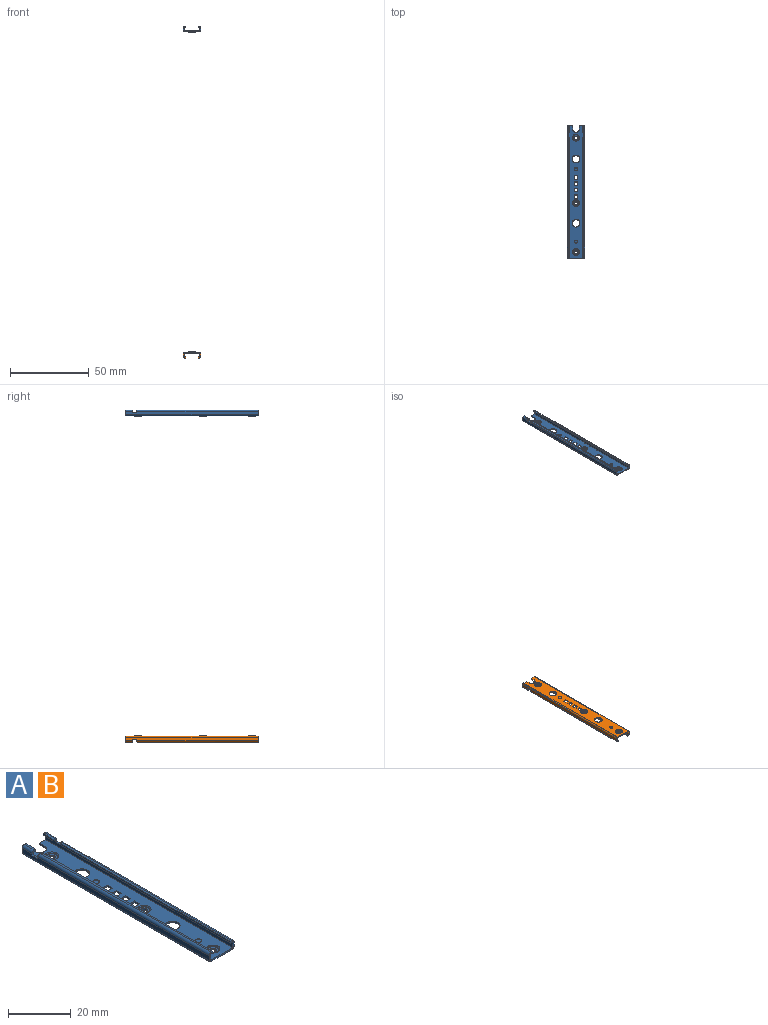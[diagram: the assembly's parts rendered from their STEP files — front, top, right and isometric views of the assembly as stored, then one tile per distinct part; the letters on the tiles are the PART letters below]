
ASSEMBLY  parts=2 mates=1
PART A: 85 faces, bbox 11.2x84.3x4 mm
  f0: plane 84.3x1.75mm, normal (-1,0,0), area 145.8mm2, adj f13,f14,f22,f51,f78,f79,f82,f84
  f1: plane 84.3x2.29mm, normal (1,0,0), area 190.3mm2, adj f2,f9,f22,f24,f78,f79,f82,f84
  f2: plane 84.3x9.9mm, normal (0,0,1), area 706.3mm2, adj f1,f10,f18,f22,f26,f27,f28,f29
  f3: plane 84.3x9.6mm, normal (0,0,-1), area 681.4mm2, adj f14,f18,f22,f26,f27,f28,f29,f30
  f4: plane 84.3x1.75mm, normal (1,0,0), area 145.8mm2, adj f12,f18,f49,f50,f80,f81,f83,f84
  f5: plane 76.91x0.7mm, normal (0,0,1), area 53.6mm2, adj f8,f13,f82,f84
  f6: plane 76.91x0.7mm, normal (0,0,1), area 53.6mm2, adj f7,f12,f83,f84
  f7: plane 75.54x0.66mm, normal (-1,0,0), area 49.9mm2, adj f6,f11,f83,f84
  f8: plane 75.54x0.66mm, normal (1,0,0), area 49.9mm2, adj f5,f9,f82,f84
  f9: plane 77.11x1.05mm, normal (0,0,-1), area 80.5mm2, adj f1,f8,f82,f84
  f10: plane 84.3x2.29mm, normal (-1,0,0), area 190.3mm2, adj f2,f11,f18,f25,f80,f81,f83,f84
  f11: plane 77.11x1.05mm, normal (0,0,-1), area 80.5mm2, adj f7,f10,f83,f84
  f12: cylinder r=1mm len=77.24mm, axis (0,-1,0), area 121.2mm2, adj f4,f6,f83,f84
  f13: cylinder r=1mm len=77.24mm, axis (0,1,0), area 121.2mm2, adj f0,f5,f82,f84
  f14: cylinder r=0.8mm len=84.3mm, axis (0,-1,0), area 105.9mm2, adj f0,f3,f22,f84
  f15: cylinder r=1.07mm len=2.14mm, axis (0,0,1), area 4mm2, adj f35,f44
  f16: cylinder r=1.07mm len=2.14mm, axis (0,0,1), area 4mm2, adj f33,f42
  f17: cylinder r=1.07mm len=2.14mm, axis (0,0,1), area 4mm2, adj f31,f40
  f18: plane 3.55x3.44mm, normal (0,1,0), area 4.3mm2, adj f2,f3,f4,f10,f19,f23,f25,f26
  f19: plane 4.45x0.66mm, normal (-1,0,0), area 2.9mm2, adj f18,f23,f25,f81
  f20: plane 4.45x0.66mm, normal (1,0,0), area 2.9mm2, adj f21,f22,f24,f78
  f21: plane 4.45x0.7mm, normal (0,0,1), area 3.1mm2, adj f20,f22,f51,f78
  f22: plane 3.55x3.44mm, normal (0,1,0), area 4.3mm2, adj f0,f1,f2,f3,f14,f20,f21,f24
  f23: plane 4.45x0.7mm, normal (0,0,1), area 3.1mm2, adj f18,f19,f50,f81
  f24: plane 4.45x1.05mm, normal (0,0,-1), area 4.7mm2, adj f1,f20,f22,f78
  f25: plane 4.45x1.05mm, normal (0,0,-1), area 4.7mm2, adj f10,f18,f19,f81
  f26: plane 2.3x0.6mm, normal (-1,0,0), area 1.4mm2, adj f2,f3,f18,f28
  f27: plane 2.3x0.6mm, normal (1,0,0), area 1.4mm2, adj f2,f3,f22,f28
  f28: cylinder r=2.17mm len=4.33mm, axis (0,0,1), area 4.1mm2, adj f2,f3,f26,f27
  f29: cylinder r=2.46mm len=4.91mm, axis (0,0,1), area 9.3mm2, adj f2,f3
  f30: cylinder r=2.46mm len=4.91mm, axis (0,0,1), area 9.3mm2, adj f2,f3
  f31: plane 3.8x3.8mm, normal (0,0,-1), area 7.7mm2, adj f17,f39
  f32: cylinder r=2.2mm len=4.4mm, axis (0,0,1), area 2.5mm2, adj f3,f39
  f33: plane 3.8x3.8mm, normal (0,0,-1), area 7.7mm2, adj f16,f38
  f34: cylinder r=2.2mm len=4.4mm, axis (0,0,1), area 2.5mm2, adj f3,f38
  f35: plane 3.8x3.8mm, normal (0,0,-1), area 7.7mm2, adj f15,f37
  f36: cylinder r=2.2mm len=4.4mm, axis (0,0,1), area 2.5mm2, adj f3,f37
  f37: torus R=1.9mm, axis (0,0,-1), area 6.2mm2, adj f35,f36
  f38: torus R=1.9mm, axis (0,0,-1), area 6.2mm2, adj f33,f34
  f39: torus R=1.9mm, axis (0,0,-1), area 6.2mm2, adj f31,f32
  f40: plane 3.81x3.81mm, normal (0,0,1), area 7.8mm2, adj f17,f41
  f41: cylinder r=1.91mm len=3.81mm, axis (0,0,1), area 2.2mm2, adj f40,f48
  f42: plane 3.81x3.81mm, normal (0,0,1), area 7.8mm2, adj f16,f43
  f43: cylinder r=1.91mm len=3.81mm, axis (0,0,1), area 2.2mm2, adj f42,f47
  f44: plane 3.81x3.81mm, normal (0,0,1), area 7.8mm2, adj f15,f45
  f45: cylinder r=1.91mm len=3.81mm, axis (0,0,1), area 2.2mm2, adj f44,f46
  f46: torus R=2.21mm, axis (0,0,1), area 6mm2, adj f2,f45
  f47: torus R=2.21mm, axis (0,0,1), area 6mm2, adj f2,f43
  f48: torus R=2.21mm, axis (0,0,1), area 6mm2, adj f2,f41
  f49: cylinder r=0.8mm len=84.3mm, axis (0,1,0), area 105.9mm2, adj f3,f4,f18,f84
  f50: cylinder r=1mm len=4.45mm, axis (0,-1,0), area 7mm2, adj f4,f18,f23,f81
  f51: cylinder r=1mm len=4.45mm, axis (0,1,0), area 7mm2, adj f0,f21,f22,f78
  f52: cylinder r=1mm len=2mm, axis (0,0,1), area 0.6mm2, adj f3,f57
  f53: plane 1.8x1.8mm, normal (0,0,-1), area 2.5mm2, adj f57
  f54: cylinder r=1mm len=2mm, axis (0,0,1), area 0.6mm2, adj f3,f56
  f55: plane 1.8x1.8mm, normal (0,0,-1), area 2.5mm2, adj f56
  f56: torus R=0.9mm, axis (0,0,-1), area 1mm2, adj f54,f55
  f57: torus R=0.9mm, axis (0,0,-1), area 1mm2, adj f52,f53
  f58: plane 2.26x0.6mm, normal (0,-1,0), area 1.4mm2, adj f2,f3,f59,f61
  f59: plane 2.3x0.6mm, normal (-1,0,0), area 1.4mm2, adj f2,f3,f58,f60
  f60: plane 2.26x0.6mm, normal (0,1,0), area 1.4mm2, adj f2,f3,f59,f61
  f61: plane 2.3x0.6mm, normal (1,0,0), area 1.4mm2, adj f2,f3,f58,f60
  f62: plane 2.26x0.6mm, normal (0,-1,0), area 1.4mm2, adj f2,f3,f63,f65
  f63: plane 2.3x0.6mm, normal (-1,0,0), area 1.4mm2, adj f2,f3,f62,f64
  f64: plane 2.26x0.6mm, normal (0,1,0), area 1.4mm2, adj f2,f3,f63,f65
  f65: plane 2.3x0.6mm, normal (1,0,0), area 1.4mm2, adj f2,f3,f62,f64
  f66: plane 2.26x0.6mm, normal (0,-1,0), area 1.4mm2, adj f2,f3,f67,f69
  f67: plane 2.3x0.6mm, normal (-1,0,0), area 1.4mm2, adj f2,f3,f66,f68
  f68: plane 2.26x0.6mm, normal (0,1,0), area 1.4mm2, adj f2,f3,f67,f69
  f69: plane 2.3x0.6mm, normal (1,0,0), area 1.4mm2, adj f2,f3,f66,f68
  f70: plane 2.26x0.6mm, normal (0,-1,0), area 1.4mm2, adj f2,f3,f71,f73
  f71: plane 2.3x0.6mm, normal (-1,0,0), area 1.4mm2, adj f2,f3,f70,f72
  f72: plane 2.26x0.6mm, normal (0,1,0), area 1.4mm2, adj f2,f3,f71,f73
  f73: plane 2.3x0.6mm, normal (1,0,0), area 1.4mm2, adj f2,f3,f70,f72
  f74: cylinder r=1.02mm len=2.03mm, axis (0,0,1), area 1.3mm2, adj f2,f75
  f75: plane 2.03x2.03mm, normal (0,0,1), area 3.2mm2, adj f74
  f76: cylinder r=1.02mm len=2.03mm, axis (0,0,1), area 1.3mm2, adj f2,f77
  f77: plane 2.03x2.03mm, normal (0,0,1), area 3.2mm2, adj f76
  f78: plane 1.7x1.65mm, normal (0,-1,0), area 1.6mm2, adj f0,f1,f20,f21,f24,f51,f79
  f79: plane 2.74x0.65mm, normal (0,0,1), area 1.7mm2, adj f0,f1,f78,f82
  f80: plane 2.74x0.65mm, normal (0,0,1), area 1.7mm2, adj f4,f10,f81,f83
  f81: plane 1.7x1.65mm, normal (0,-1,0), area 1.6mm2, adj f4,f10,f19,f23,f25,f50,f80
  f82: cylinder r=1.7mm len=1.7mm, axis (0,0,1), area 2.2mm2, adj f0,f1,f5,f8,f9,f13,f79
  f83: cylinder r=1.7mm len=1.7mm, axis (0,0,-1), area 2.2mm2, adj f4,f6,f7,f10,f11,f12,f80
  f84: plane 11.2x3.55mm, normal (0,-1,0), area 11.2mm2, adj f0,f1,f2,f3,f4,f5,f6,f7
PART B: same geometry as A
PLACE A t=(431.27,274.71,141.96)mm
PLACE B rot(axis=(0,1,0),180deg) t=(431.64,274.71,-61.9)mm
MATE fastened B.f17 <-> A.f17  axis (0,0,-1) through (431.45,311.29,-61.42)mm
